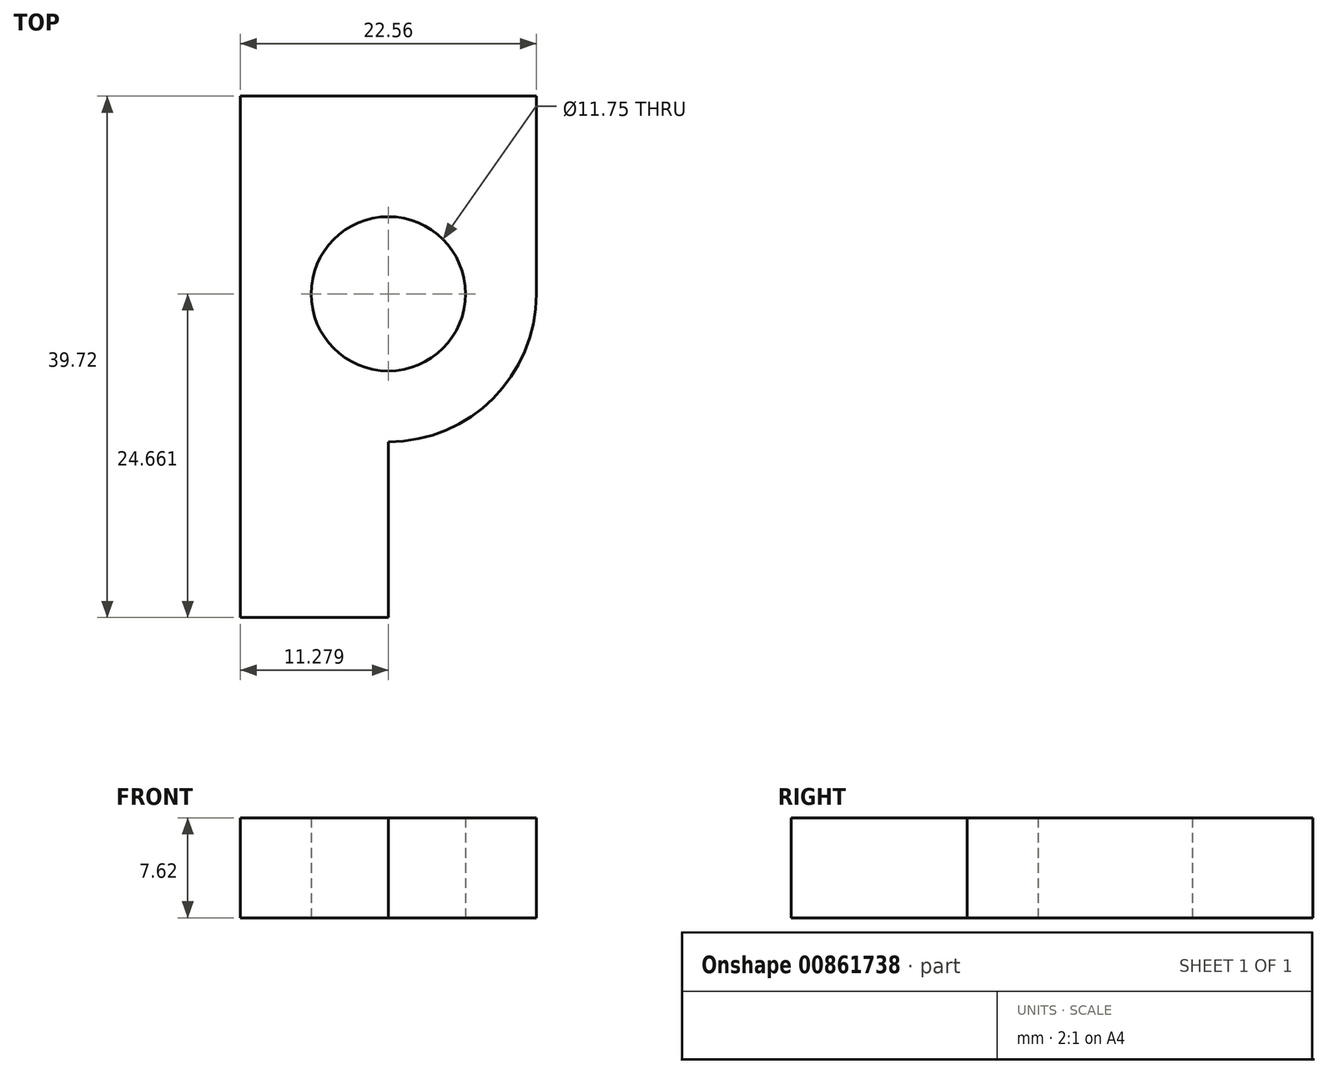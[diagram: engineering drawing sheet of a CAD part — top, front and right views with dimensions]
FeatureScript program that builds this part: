
annotation { "Feature Type Name" : "Feature", "Feature Type Description" : "" }
export const myFeature = defineFeature(function(context is Context, id is Id, definition is map)
    precondition{}
    {
        {
            var Q0;
            Q0=qCreatedBy(makeId("Top.planeOp"),FACE);
            var sketch = newSketch(context, id + "F0", { "sketchPlane" : qUnion([Q0])});
            skLineSegment(sketch, "E0.bottom", {"start": v(-17.73, 24.66) * mm, "end": v(-6.45, 24.66) * mm});
            skLineSegment(sketch, "E0.top", {"start": v(-17.73, 0) * mm, "end": v(-6.45, 0) * mm});
            skLineSegment(sketch, "E0.left", {"start": v(-17.73, 24.66) * mm, "end": v(-17.73, 0) * mm});
            skLineSegment(sketch, "E0.right", {"start": v(-6.45, 24.66) * mm, "end": v(-6.45, 0) * mm});
            skCircle(sketch, "E1", {"center": v(-6.45, 24.66) * mm, "radius": 11.28 * mm});
            skCircle(sketch, "E2", {"center": v(-6.45, 24.66) * mm, "radius": 5.87 * mm});
            skLineSegment(sketch, "E3.bottom", {"start": v(-17.73, 24.66) * mm, "end": v(4.83, 24.66) * mm});
            skLineSegment(sketch, "E3.top", {"start": v(-17.73, 24.66) * mm, "end": v(4.83, 24.66) * mm});
            skLineSegment(sketch, "E3.left", {"start": v(-17.73, 24.66) * mm, "end": v(-17.73, 24.66) * mm});
            skLineSegment(sketch, "E3.right", {"start": v(4.83, 24.66) * mm, "end": v(4.83, 24.66) * mm});
            skLineSegment(sketch, "E4.bottom", {"start": v(4.83, 24.66) * mm, "end": v(-17.73, 24.66) * mm});
            skLineSegment(sketch, "E4.top", {"start": v(4.83, 39.72) * mm, "end": v(-17.73, 39.72) * mm});
            skLineSegment(sketch, "E4.left", {"start": v(4.83, 24.66) * mm, "end": v(4.83, 39.72) * mm});
            skLineSegment(sketch, "E4.right", {"start": v(-17.73, 24.66) * mm, "end": v(-17.73, 39.72) * mm});
            skSolve(sketch);
        }
        {
            var Q0;
            {var subQ0=sQuery(id+"F0.wireOp",EDGE,"E0.top");Q0=makeQuery(id+"F0.imprint","IMPRINT",FACE,{"disambiguationData":[TD([[makeQuery(id+"F0.imprint","IMPRINT",EDGE,{"derivedFrom":subQ0}),1.0]])]});}
            extrude(context, id + "F1", {"entities" : qUnion([Q0]), "depth" : 6.35 * mm, "offsetDistance" : 25.4 * mm});
        }
        {
            var Q0;
            Q0 = qSketchRegion(id + "F0", true);
            extrude(context, id + "F2", {"entities" : qUnion([Q0]), "operationType" : NewBodyOperationType.ADD, "depth" : 7.62 * mm, "offsetDistance" : 25.4 * mm});
        }
    });
